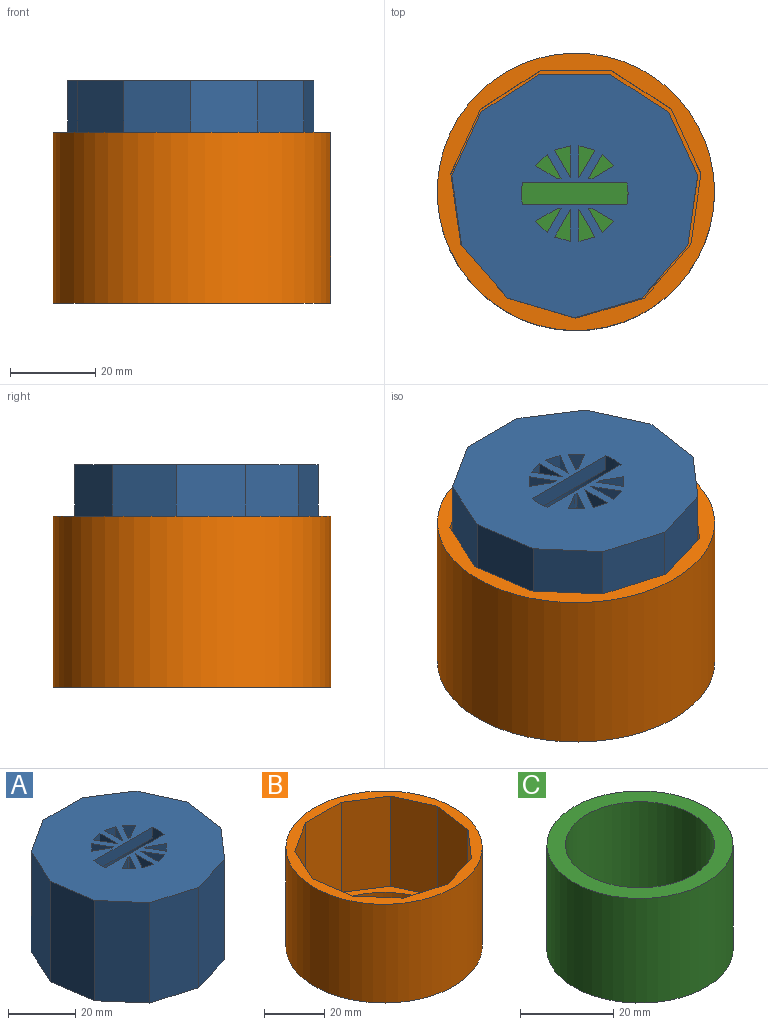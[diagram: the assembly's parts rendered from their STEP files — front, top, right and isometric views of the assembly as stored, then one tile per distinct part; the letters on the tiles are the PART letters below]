
ASSEMBLY  parts=3 mates=2
PART A: 67 faces, bbox 57.6x57.1x36.5 mm
  f0: cylinder r=12.5mm len=36.5mm, axis (0,0,-1), area 2592.8mm2, adj f22,f23,f49,f50,f51,f52
  f1: cylinder r=25.1mm len=50.2mm, axis (0,0,-1), area 2958.5mm2, adj f2,f3,f4,f5,f8,f10,f11,f12
  f2: cylinder r=25.1mm len=39.55mm, axis (0,0,-1), area 375mm2, adj f1,f5,f7
  f3: cylinder r=25.1mm len=26.9mm, axis (0,0,-1), area 213.3mm2, adj f1,f5,f9
  f4: cylinder r=25.1mm len=12.33mm, axis (0,0,-1), area 40.1mm2, adj f1,f5
  f5: plane 50.2x50.2mm, normal (0,0,-1), area 1091.9mm2, adj f1,f2,f3,f4,f6,f7,f9,f11
  f6: cylinder r=16.5mm len=33.87mm, axis (0,0,-1), area 3511.3mm2, adj f5,f22
  f7: plane 3.76x3.41mm, normal (0.97,-0.22,0), area 11.6mm2, adj f2,f5
  f8: plane 4.78x2.97mm, normal (0.85,0.53,0), area 14.1mm2, adj f1
  f9: plane 3.76x3.16mm, normal (0.43,-0.9,0), area 11.6mm2, adj f3,f5
  f10: plane 4.78x3.31mm, normal (0.94,-0.33,0), area 14.1mm2, adj f1
  f11: plane 3.76x3.41mm, normal (-0.97,-0.22,0), area 11.6mm2, adj f1,f5
  f12: plane 4.78x2.97mm, normal (-0.53,-0.85,0), area 14.1mm2, adj f1
  f13: plane 3.76x2.74mm, normal (-0.78,0.62,0), area 11.6mm2, adj f1,f5
  f14: plane 4.78x3.48mm, normal (-0.99,-0.11,0), area 14.1mm2, adj f1
  f15: plane 3.76x3.16mm, normal (-0.43,-0.9,0), area 11.6mm2, adj f1,f5
  f16: plane 4.78x3.31mm, normal (0.33,-0.94,0), area 14.1mm2, adj f1
  f17: plane 3.76x2.74mm, normal (0.78,0.62,0), area 11.6mm2, adj f1,f5
  f18: plane 4.78x3.48mm, normal (0.11,0.99,0), area 14.1mm2, adj f1
  f19: plane 3.76x3.5mm, normal (0,1,0), area 11.6mm2, adj f1,f5
  f20: plane 4.78x2.48mm, normal (-0.71,0.71,0), area 14.1mm2, adj f1
  f21: plane 57.65x57.06mm, normal (0,0,-1), area 542.1mm2, adj f1,f24,f25,f26,f27,f28,f29,f30
  f22: plane 33x33mm, normal (0,0,-1), area 364.4mm2, adj f0,f6
  f23: plane 57.65x57.06mm, normal (0,0,1), area 2287.1mm2, adj f0,f24,f25,f26,f27,f28,f29,f30
  f24: plane 36.5x12.4mm, normal (-0.76,-0.65,0), area 598.9mm2, adj f21,f23,f25,f34
  f25: plane 36.5x15.74mm, normal (-0.28,-0.96,0), area 598.9mm2, adj f21,f23,f24,f26
  f26: plane 36.5x15.74mm, normal (0.28,-0.96,0), area 598.9mm2, adj f21,f23,f25,f27
  f27: plane 36.5x12.4mm, normal (0.76,-0.65,0), area 598.9mm2, adj f21,f23,f26,f28
  f28: plane 36.5x16.24mm, normal (0.99,-0.14,0), area 598.9mm2, adj f21,f23,f27,f29
  f29: plane 36.5x14.93mm, normal (0.91,0.42,0), area 598.9mm2, adj f21,f23,f28,f30
  f30: plane 36.5x13.8mm, normal (0.54,0.84,0), area 598.9mm2, adj f21,f23,f29,f31
  f31: plane 36.5x16.41mm, normal (0,1,0), area 598.9mm2, adj f21,f23,f30,f32
  f32: plane 36.5x13.8mm, normal (-0.54,0.84,0), area 598.9mm2, adj f21,f23,f31,f33
  f33: plane 36.5x14.93mm, normal (-0.91,0.42,0), area 598.9mm2, adj f21,f23,f32,f34
  f34: plane 36.5x16.24mm, normal (-0.99,-0.14,0), area 598.9mm2, adj f21,f23,f24,f33
  f35: plane 4x3.73mm, normal (-0.26,0.97,0), area 15.5mm2, adj f23,f36,f37,f49
  f36: plane 7.46x4mm, normal (1,0,0), area 29.9mm2, adj f23,f35,f37,f49
  f37: plane 6.46x4mm, normal (-0.87,-0.5,0), area 29.9mm2, adj f23,f35,f36,f49
  f38: plane 4x2.73mm, normal (0.71,0.71,0), area 15.5mm2, adj f23,f39,f41,f49
  f39: plane 5.13x4mm, normal (0.5,-0.87,0), area 23.7mm2, adj f23,f38,f40,f49
  f40: plane 4x0.89mm, normal (0,-1,0), area 3.5mm2, adj f23,f39,f41,f49
  f41: plane 5.7x4mm, normal (-0.87,0.5,0), area 26.3mm2, adj f23,f38,f40,f49
  f42: plane 6.46x4mm, normal (0.87,-0.5,0), area 29.9mm2, adj f23,f43,f44,f49
  f43: plane 7.46x4mm, normal (-1,0,0), area 29.9mm2, adj f23,f42,f44,f49
  f44: plane 4x3.73mm, normal (0.26,0.97,0), area 15.5mm2, adj f23,f42,f43,f49
  f45: plane 5.7x4mm, normal (0.87,0.5,0), area 26.3mm2, adj f23,f46,f48,f49
  f46: plane 4x0.89mm, normal (0,-1,0), area 3.5mm2, adj f23,f45,f47,f49
  f47: plane 5.13x4mm, normal (-0.5,-0.87,0), area 23.7mm2, adj f23,f46,f48,f49
  f48: plane 4x2.73mm, normal (-0.71,0.71,0), area 15.5mm2, adj f23,f45,f47,f49
  f49: plane 24.5x10mm, normal (0,0,-1), area 128.3mm2, adj f0,f35,f36,f37,f38,f39,f40,f41
  f50: plane 24.5x4mm, normal (0,1,0), area 98mm2, adj f0,f23,f49
  f51: plane 24.5x10mm, normal (0,0,-1), area 128.3mm2, adj f0,f52,f53,f54,f55,f56,f57,f58
  f52: plane 24.5x4mm, normal (0,-1,0), area 98mm2, adj f0,f23,f51
  f53: plane 7.46x4mm, normal (1,0,0), area 29.9mm2, adj f23,f51,f54,f63
  f54: plane 4x3.73mm, normal (-0.26,-0.97,0), area 15.5mm2, adj f23,f51,f53,f63
  f55: plane 5.13x4mm, normal (0.5,0.87,0), area 23.7mm2, adj f23,f51,f56,f64
  f56: plane 4x2.73mm, normal (0.71,-0.71,0), area 15.5mm2, adj f23,f51,f55,f57
  f57: plane 5.7x4mm, normal (-0.87,-0.5,0), area 26.3mm2, adj f23,f51,f56,f64
  f58: plane 5.7x4mm, normal (0.87,-0.5,0), area 26.3mm2, adj f23,f51,f59,f65
  f59: plane 4x2.73mm, normal (-0.71,-0.71,0), area 15.5mm2, adj f23,f51,f58,f60
  f60: plane 5.13x4mm, normal (-0.5,0.87,0), area 23.7mm2, adj f23,f51,f59,f65
  f61: plane 4x3.73mm, normal (0.26,-0.97,0), area 15.5mm2, adj f23,f51,f62,f66
  f62: plane 7.46x4mm, normal (-1,0,0), area 29.9mm2, adj f23,f51,f61,f66
  f63: plane 6.46x4mm, normal (-0.87,0.5,0), area 29.9mm2, adj f23,f51,f53,f54
  f64: plane 4x0.89mm, normal (0,1,0), area 3.5mm2, adj f23,f51,f55,f57
  f65: plane 4x0.89mm, normal (0,1,0), area 3.5mm2, adj f23,f51,f58,f60
  f66: plane 6.46x4mm, normal (0.87,0.5,0), area 29.9mm2, adj f23,f51,f61,f62
PART B: 16 faces, bbox 65x65x40 mm
  f0: plane 36.5x16.01mm, normal (0.28,0.96,0), area 609.2mm2, adj f1,f10,f13,f14
  f1: plane 36.5x12.61mm, normal (0.76,0.65,0), area 609.2mm2, adj f0,f2,f13,f14
  f2: plane 36.5x16.52mm, normal (0.99,0.14,0), area 609.2mm2, adj f1,f3,f13,f14
  f3: plane 36.5x15.18mm, normal (0.91,-0.42,0), area 609.2mm2, adj f2,f4,f13,f14
  f4: plane 36.5x14.04mm, normal (0.54,-0.84,0), area 609.2mm2, adj f3,f5,f13,f14
  f5: plane 36.5x16.69mm, normal (0,-1,0), area 609.2mm2, adj f4,f6,f13,f14
  f6: plane 36.5x14.04mm, normal (-0.54,-0.84,0), area 609.2mm2, adj f5,f7,f13,f14
  f7: plane 36.5x15.18mm, normal (-0.91,-0.42,0), area 609.2mm2, adj f6,f8,f13,f14
  f8: plane 36.5x16.52mm, normal (-0.99,0.14,0), area 609.2mm2, adj f7,f9,f13,f14
  f9: plane 36.5x12.61mm, normal (-0.76,0.65,0), area 609.2mm2, adj f8,f10,f13,f14
  f10: plane 36.5x16.01mm, normal (-0.28,0.96,0), area 609.2mm2, adj f0,f9,f13,f14
  f11: cylinder r=32.5mm len=65mm, axis (0,0,1), area 8168.1mm2, adj f12,f13
  f12: plane 65x65mm, normal (0,0,-1), area 1194.6mm2, adj f11,f15
  f13: plane 65x65mm, normal (0,0,1), area 709.6mm2, adj f0,f1,f2,f3,f4,f5,f6,f7
  f14: plane 58.64x58.04mm, normal (0,0,1), area 485mm2, adj f0,f1,f2,f3,f4,f5,f6,f7
  f15: cylinder r=26mm len=52mm, axis (0,0,-1), area 571.8mm2, adj f12,f14
PART C: 5 faces, bbox 40x40x27.5 mm
  f0: cylinder r=20mm len=40mm, axis (0,0,-1), area 3455.8mm2, adj f1,f2
  f1: plane 40x40mm, normal (0,0,-1), area 1256.6mm2, adj f0
  f2: plane 40x40mm, normal (0,0,1), area 452.4mm2, adj f0,f4
  f3: plane 32x32mm, normal (0,0,1), area 804.2mm2, adj f4
  f4: cylinder r=16mm len=32mm, axis (0,0,-1), area 2563.5mm2, adj f2,f3
PLACE A t=(-0.27,-0.42,12.11)mm
PLACE B at identity fixed
PLACE C rot(axis=(0,0,-1),68.3deg) t=(-0.27,-0.42,-0.36)mm
MATE cylindrical C.f0 <-> A.f0  axis (0,0,1) through (-0.27,-0.42,39.78)mm
MATE slider A.f23 <-> B.f13  axis (0,0,1) through (-16.01,-24.92,61.11)mm
